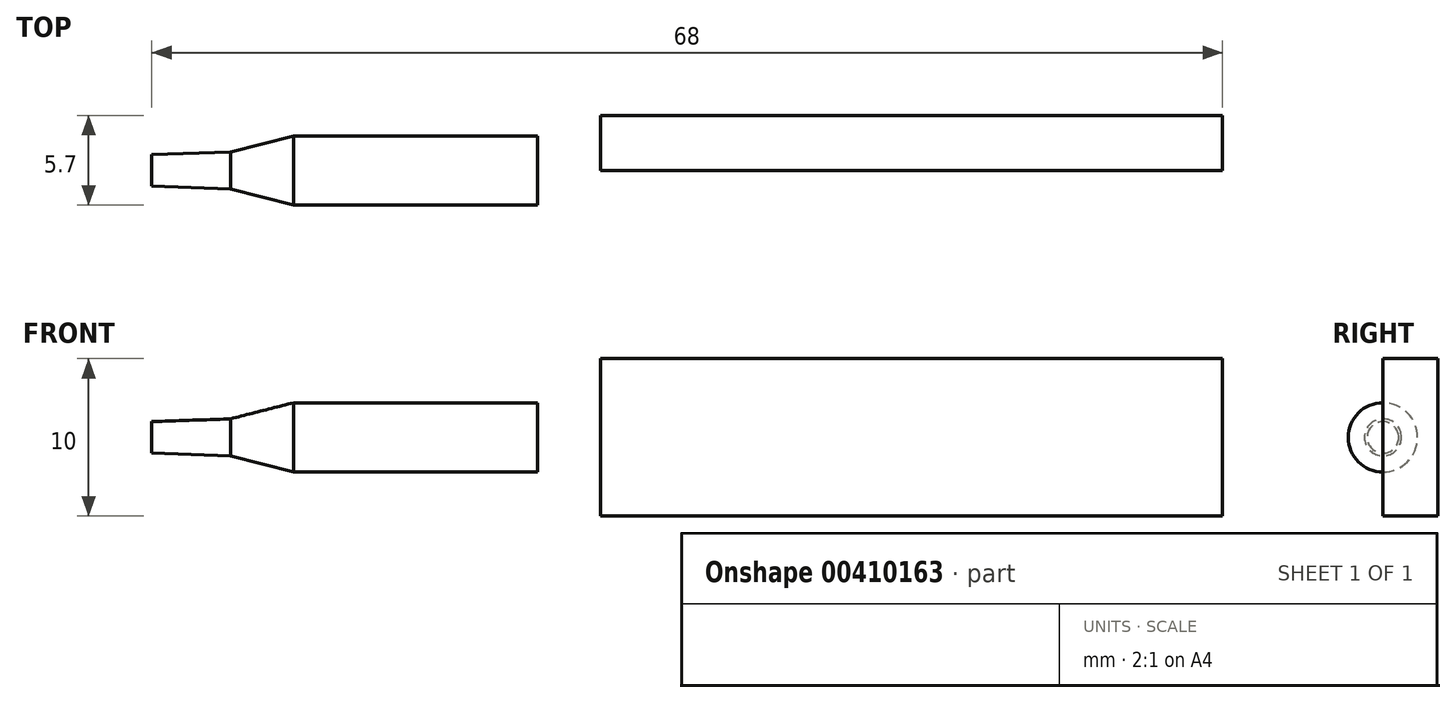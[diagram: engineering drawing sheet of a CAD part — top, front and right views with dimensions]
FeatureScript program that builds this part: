
annotation { "Feature Type Name" : "Feature", "Feature Type Description" : "" }
export const myFeature = defineFeature(function(context is Context, id is Id, definition is map)
    precondition{}
    {
        {
            var Q0;
            Q0=qCreatedBy(makeId("Front.planeOp"),FACE);
            var sketch = newSketch(context, id + "F0", { "sketchPlane" : qUnion([Q0])});
            skLineSegment(sketch, "E0", {"start": v(-65.71, 0) * mm, "end": v(-65.71, 1) * mm});
            skLineSegment(sketch, "E1", {"start": v(-65.71, 1) * mm, "end": v(-60.71, 1.17) * mm});
            skLineSegment(sketch, "E2", {"start": v(-60.71, 1.17) * mm, "end": v(-56.71, 2.2) * mm});
            skLineSegment(sketch, "E3", {"start": v(-56.71, 2.2) * mm, "end": v(-41.21, 2.2) * mm});
            skLineSegment(sketch, "E4", {"start": v(-41.21, 2.2) * mm, "end": v(-37.21, 5) * mm});
            skLineSegment(sketch, "E5", {"start": v(-37.21, 5) * mm, "end": v(2.29, 5) * mm});
            skLineSegment(sketch, "E6", {"start": v(2.29, 5) * mm, "end": v(2.29, 0) * mm});
            skLineSegment(sketch, "E7", {"start": v(-65.71, 0) * mm, "end": v(2.29, 0) * mm});
            skLineSegment(sketch, "E8", {"start": v(-41.21, 2.2) * mm, "end": v(-41.21, 0) * mm});
            skLineSegment(sketch, "E9", {"start": v(-65.71, 0) * mm, "end": v(-41.21, 0) * mm});
            skLineSegment(sketch, "E10.MirrorCS", {"start": v(-41.21, -2.2) * mm, "end": v(-37.21, -5) * mm});
            skLineSegment(sketch, "E11.MirrorCS", {"start": v(-37.21, -5) * mm, "end": v(2.29, -5) * mm});
            skLineSegment(sketch, "E12.MirrorCS", {"start": v(2.29, -5) * mm, "end": v(2.29, 0) * mm});
            skLineSegment(sketch, "E13.MirrorCS", {"start": v(-41.21, -2.2) * mm, "end": v(-41.21, 0) * mm});
            skLineSegment(sketch, "E14", {"start": v(-37.21, 5) * mm, "end": v(-37.21, -5) * mm});
            skSolve(sketch);
        }
        {
            var Q0;
            Q0=makeQuery(id+"F0.imprint","IMPRINT",FACE,{"disambiguationData":[TD([[makeQuery(id+"F0.imprint","IMPRINT",EDGE,{"derivedFrom":sQuery(id+"F0.wireOp",EDGE,"E0")}),-1.0]])]});
            var Q1;
            Q1=sQuery(id+"F0.wireOp",EDGE,"E9");
            revolve(context, id + "F1", {"entities" : qUnion([Q0]), "axis" : qUnion([Q1]), "revolveType" : RevolveType.FULL});
        }
        {
            var Q0;
            {var subQ0=sQuery(id+"F0.wireOp",EDGE,"E5");Q0=makeQuery(id+"F0.imprint","IMPRINT",FACE,{"disambiguationData":[TD([[makeQuery(id+"F0.imprint","IMPRINT",EDGE,{"derivedFrom":subQ0}),-1.0]])]});}
            var Q1;
            {var subQ4=sQuery(id+"F0.wireOp",EDGE,"E11.MirrorCS");Q1=makeQuery(id+"F0.imprint","IMPRINT",FACE,{"disambiguationData":[TD([[makeQuery(id+"F0.imprint","IMPRINT",EDGE,{"derivedFrom":subQ4}),1.0]])]});}
            extrude(context, id + "F2", {"entities" : qUnion([Q0, Q1]), "oppositeDirection" : true, "depth" : 3.5 * mm});
        }
    });
